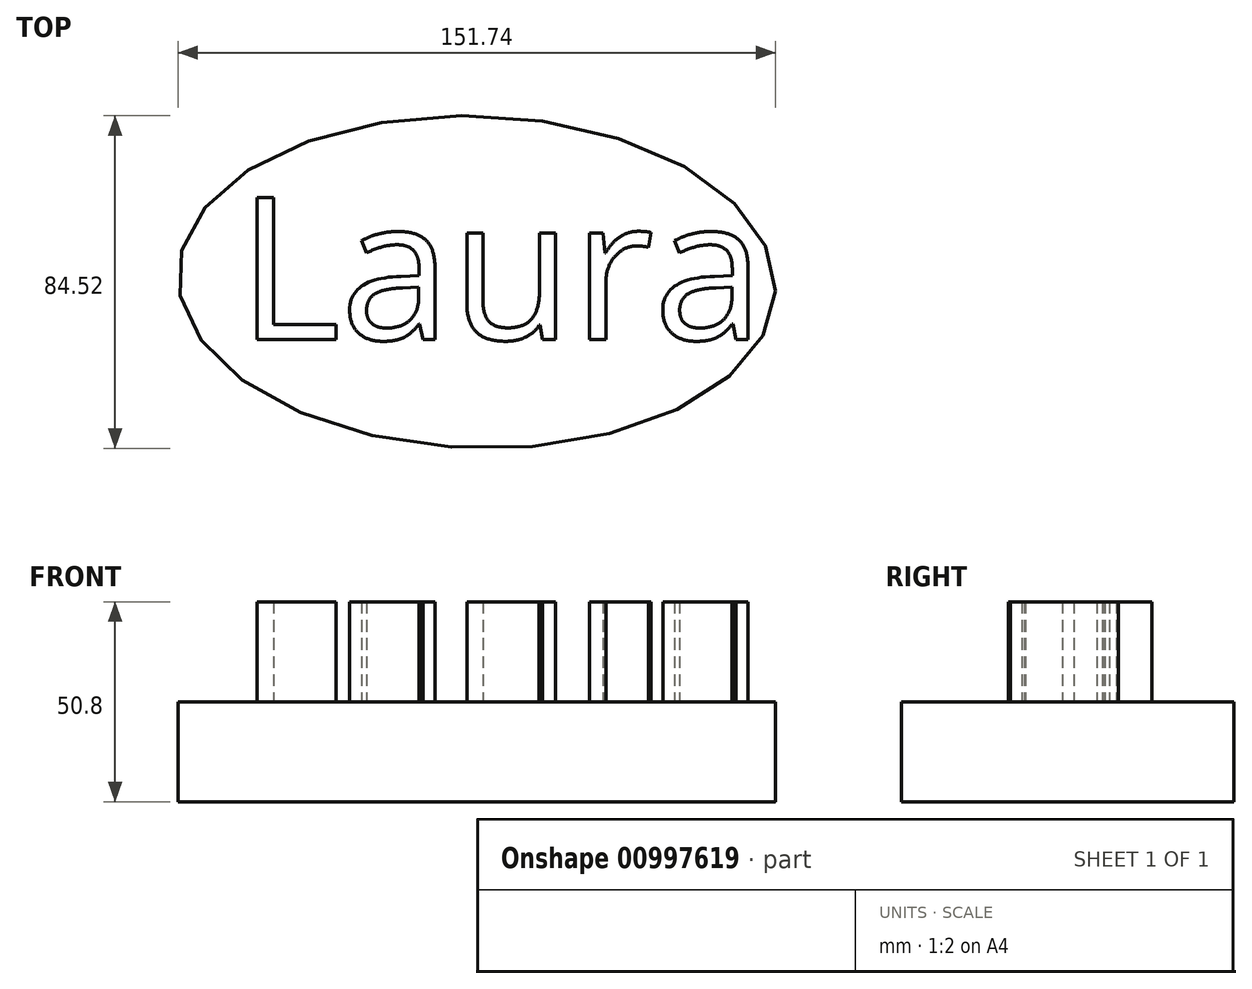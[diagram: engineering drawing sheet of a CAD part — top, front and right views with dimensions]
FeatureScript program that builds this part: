
annotation { "Feature Type Name" : "Feature", "Feature Type Description" : "" }
export const myFeature = defineFeature(function(context is Context, id is Id, definition is map)
    precondition{}
    {
        {
            var Q0;
            Q0=qCreatedBy(makeId("Top.planeOp"),FACE);
            var sketch = newSketch(context, id + "F0", { "sketchPlane" : qUnion([Q0])});
            skEllipse(sketch, "E0", {"center": v(0, 0) * mm, "majorRadius": 75.9 * mm, "minorRadius": 42.22 * mm, "majorAxis": v(1, -0.03)});
            skSolve(sketch);
        }
        {
            var Q0;
            Q0 = qSketchRegion(id + "F0", true);
            extrude(context, id + "F1", {"entities" : qUnion([Q0]), "depth" : 25.4 * mm, "offsetDistance" : 25.4 * mm});
        }
        {
            var Q0;
            Q0=makeQuery(id+"F1.opExtrude","CAP_FACE",FACE,{"disambiguationData":[OSD([sQuery(id+"F0.wireOp",EDGE,"E0")])],"isStart":false});
            var sketch = newSketch(context, id + "F2", { "sketchPlane" : qUnion([Q0])});
            skText(sketch, "E1", { "text": "Laura", "fontName": "OpenSans-Regular.ttf"});
            const initialGuessF2  = {"E1": [-0.06076, -0.01457, 1, 0, 0.03629]};
            skSetInitialGuess(sketch, initialGuessF2);
            skSolve(sketch);
        }
        {
            var Q0;
            Q0 = qSketchRegion(id + "F2", true);
            extrude(context, id + "F3", {"entities" : qUnion([Q0]), "operationType" : NewBodyOperationType.ADD, "depth" : 25.4 * mm, "offsetDistance" : 25.4 * mm});
        }
    });
